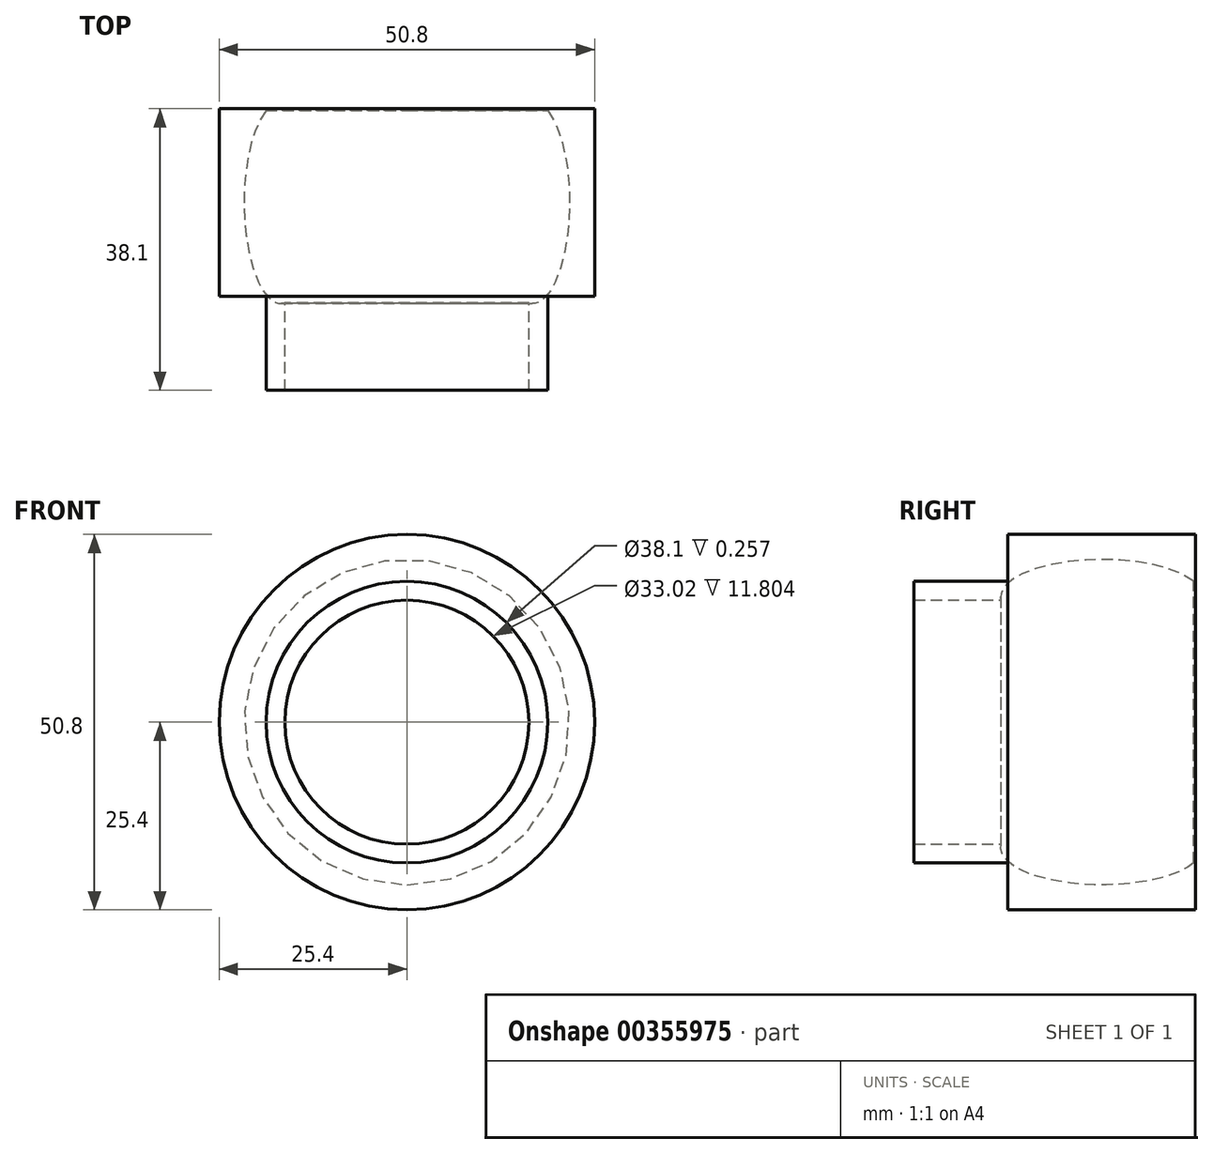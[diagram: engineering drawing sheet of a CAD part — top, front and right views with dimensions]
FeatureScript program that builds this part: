
annotation { "Feature Type Name" : "Feature", "Feature Type Description" : "" }
export const myFeature = defineFeature(function(context is Context, id is Id, definition is map)
    precondition{}
    {
        {
            var Q0;
            Q0=qCreatedBy(makeId("Front.planeOp"),FACE);
            var sketch = newSketch(context, id + "F0", { "sketchPlane" : qUnion([Q0])});
            skCircle(sketch, "E0", {"center": v(0, 0) * mm, "radius": 19.05 * mm});
            skCircle(sketch, "E1", {"center": v(0, 0) * mm, "radius": 25.4 * mm});
            skCircle(sketch, "E2.0", {"center": v(0, 0) * mm, "radius": 16.51 * mm});
            skSolve(sketch);
        }
        {
            var Q0;
            Q0=makeQuery(id+"F0.imprint","IMPRINT",FACE,{"disambiguationData":[TD([[makeQuery(id+"F0.imprint","IMPRINT",EDGE,{"derivedFrom":sQuery(id+"F0.wireOp",EDGE,"E0")}),-1.0]])]});
            extrude(context, id + "F1", {"entities" : qUnion([Q0]), "endBound" : BoundingType.SYMMETRIC, "depth" : 25.4 * mm});
        }
        {
            var Q0;
            Q0=makeQuery(id+"F0.imprint","IMPRINT",FACE,{"disambiguationData":[TD([[makeQuery(id+"F0.imprint","IMPRINT",EDGE,{"derivedFrom":sQuery(id+"F0.wireOp",EDGE,"E0")}),1.0]])]});
            extrude(context, id + "F2", {"entities" : qUnion([Q0]), "operationType" : NewBodyOperationType.ADD, "depth" : 25.4 * mm});
        }
        {
            var Q0;
            Q0=qCreatedBy(makeId("Right.planeOp"),FACE);
            var sketch = newSketch(context, id + "F3", { "sketchPlane" : qUnion([Q0])});
            skEllipse(sketch, "E3", {"center": v(0, 16.98) * mm, "majorRadius": 13.65 * mm, "minorRadius": 5.04 * mm, "majorAxis": v(1, 0)});
            skSolve(sketch);
        }
        {
            var Q0;
            Q0=qSketchRegion(id+"F3",true);
            var Q1;
            Q1=makeQuery(id+"F1.opExtrude","CAP_EDGE",EDGE,{"disambiguationData":[OSD([sQuery(id+"F0.wireOp",EDGE,"E0")])],"isStart":true});
            revolve(context, id + "F4", {"operationType" : NewBodyOperationType.REMOVE, "entities" : qUnion([Q0]), "axis" : qUnion([Q1]), "revolveType" : RevolveType.FULL, "oppositeDirection" : true});
        }
    });
